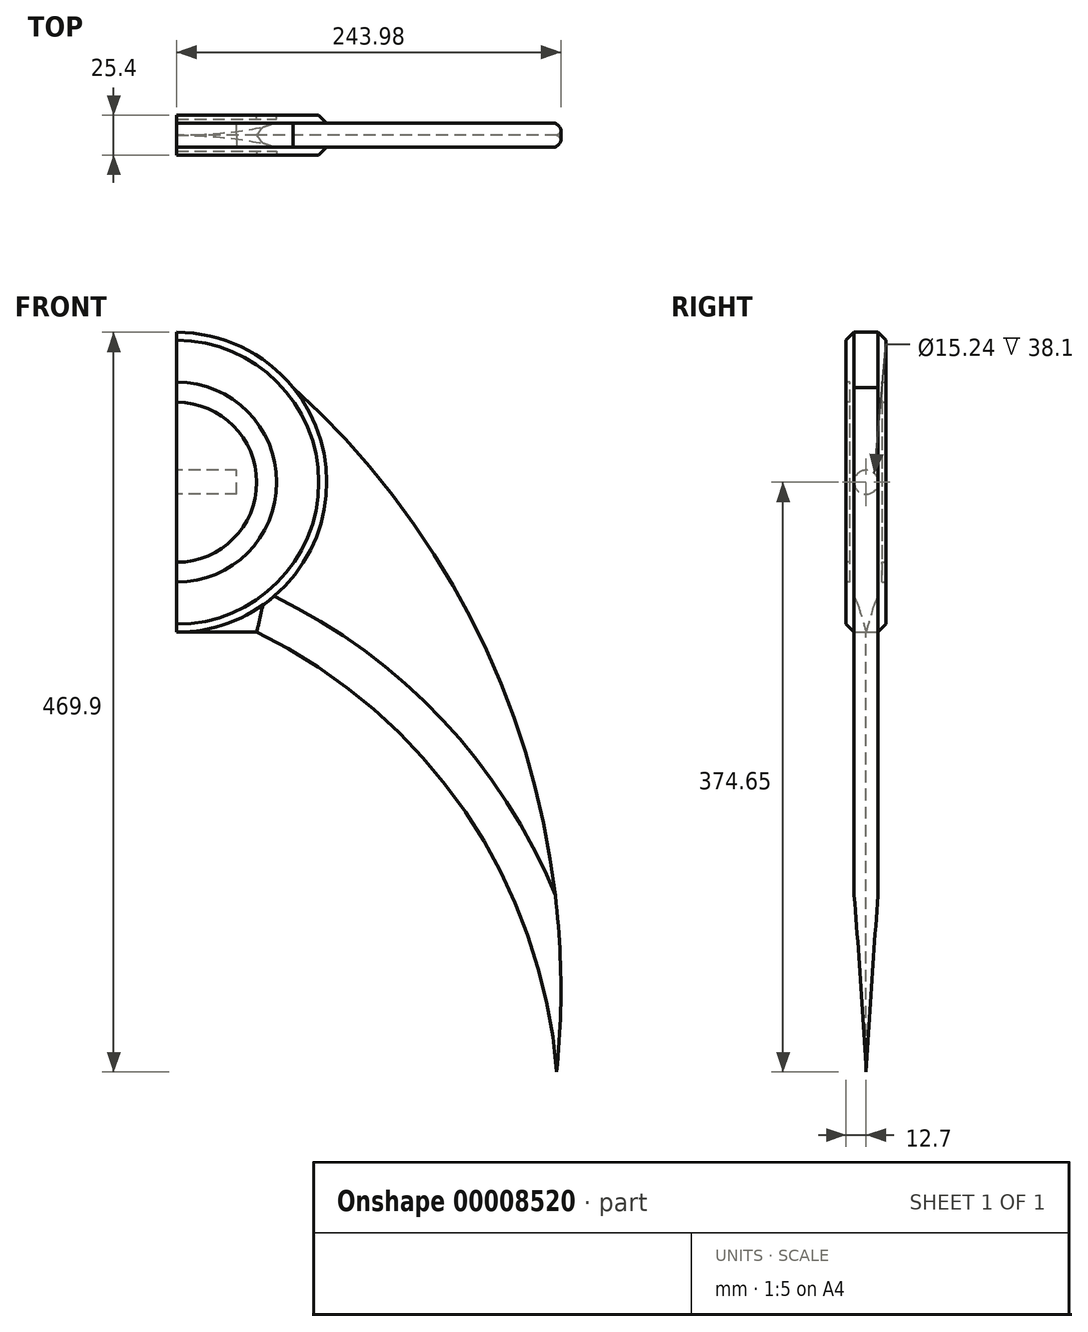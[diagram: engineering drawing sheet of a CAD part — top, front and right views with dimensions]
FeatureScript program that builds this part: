
annotation { "Feature Type Name" : "Feature", "Feature Type Description" : "" }
export const myFeature = defineFeature(function(context is Context, id is Id, definition is map)
    precondition{}
    {
        {
            var Q0;
            Q0=qCreatedBy(makeId("Right.planeOp"),FACE);
            var sketch = newSketch(context, id + "F0", { "sketchPlane" : qUnion([Q0])});
            skCircle(sketch, "E0", {"center": v(0, 0) * mm, "radius": 7.62 * mm});
            skSolve(sketch);
        }
        {
            var Q0;
            Q0=makeQuery(id+"F0.imprint","IMPRINT",FACE,{"disambiguationData":[TD([[makeQuery(id+"F0.imprint","IMPRINT",EDGE,{"derivedFrom":sQuery(id+"F0.wireOp",EDGE,"E0")}),1.0]])]});
            extrude(context, id + "F1", {"entities" : qUnion([Q0]), "depth" : 38.1 * mm});
        }
        {
            var Q0;
            Q0=qCreatedBy(makeId("Front.planeOp"),FACE);
            var sketch = newSketch(context, id + "F2", { "sketchPlane" : qUnion([Q0])});
            skLineSegment(sketch, "E1.0", {"start": v(38.1, 7.62) * mm, "end": v(38.1, -7.62) * mm});
            skArc(sketch, "E2", {"start": v(111.98, 60.11) * mm, "mid": v(79, 86.02) * mm, "end": v(38.1, 95.25) * mm});
            skLineSegment(sketch, "E3", {"start": v(38.1, 0) * mm, "end": v(38.1, 95.25) * mm});
            skLineSegment(sketch, "E4", {"start": v(38.1, 0) * mm, "end": v(38.1, -95.25) * mm});
            skLineSegment(sketch, "E5", {"start": v(38.1, -95.25) * mm, "end": v(88.9, -95.25) * mm});
            skArc(sketch, "E6", {"start": v(279.4, -374.65) * mm, "mid": v(221.44, -209.52) * mm, "end": v(88.9, -95.25) * mm});
            skArc(sketch, "E7", {"start": v(279.4, -374.65) * mm, "mid": v(247.68, -137.25) * mm, "end": v(111.98, 60.11) * mm});
            skSolve(sketch);
        }
        {
            var Q0;
            {var subQ3=sQuery(id+"F2.wireOp",EDGE,"E2");Q0=makeQuery(id+"F2.imprint","IMPRINT",FACE,{"disambiguationData":[TD([[makeQuery(id+"F2.imprint","IMPRINT",EDGE,{"derivedFrom":subQ3}),1.0]])]});}
            extrude(context, id + "F3", {"entities" : qUnion([Q0]), "operationType" : NewBodyOperationType.ADD, "depth" : 15.24 * mm, "symmetric" : true});
        }
        {
            var Q0;
            Q0=makeQuery(id+"F3.opExtrude","CAP_EDGE",EDGE,{"disambiguationData":[OSD([sQuery(id+"F2.wireOp",EDGE,"E6")])],"isStart":false});
            var Q1;
            Q1=makeQuery(id+"F3.opExtrude","CAP_EDGE",EDGE,{"disambiguationData":[OSD([sQuery(id+"F2.wireOp",EDGE,"E5")])],"isStart":false});
            chamfer(context, id + "F4", {"entities" : qUnion([Q0, Q1]), "chamferType" : ChamferType.TWO_OFFSETS, "width1" : 7.62 * mm, "oppositeDirection" : false, "width2" : 25.4 * mm, "tangentPropagation" : true});
        }
        {
            var Q0;
            Q0=makeQuery(id+"F3.opExtrude","CAP_EDGE",EDGE,{"disambiguationData":[OSD([sQuery(id+"F2.wireOp",EDGE,"E6")])],"isStart":true});
            var Q1;
            Q1=makeQuery(id+"F3.opExtrude","CAP_EDGE",EDGE,{"disambiguationData":[OSD([sQuery(id+"F2.wireOp",EDGE,"E5")])],"isStart":true});
            chamfer(context, id + "F5", {"entities" : qUnion([Q0, Q1]), "chamferType" : ChamferType.TWO_OFFSETS, "width1" : 25.4 * mm, "oppositeDirection" : false, "width2" : 7.62 * mm, "tangentPropagation" : true});
        }
        {
            var Q0;
            Q0=qCreatedBy(makeId("Front.planeOp"),FACE);
            var sketch = newSketch(context, id + "F6", { "sketchPlane" : qUnion([Q0])});
            skLineSegment(sketch, "E8.0", {"start": v(38.1, 0) * mm, "end": v(38.1, 95.25) * mm});
            skCircle(sketch, "E9", {"center": v(38.1, 0) * mm, "radius": 95.25 * mm});
            skLineSegment(sketch, "E10", {"start": v(38.1, 0) * mm, "end": v(38.1, -95.25) * mm});
            skSolve(sketch);
        }
        {
            var Q0;
            {var subQ2=sQuery(id+"F6.wireOp",EDGE,"E8.0");Q0=makeQuery(id+"F6.imprint","IMPRINT",FACE,{"disambiguationData":[TD([[makeQuery(id+"F6.imprint","IMPRINT",EDGE,{"derivedFrom":subQ2}),-1.0]])]});}
            extrude(context, id + "F7", {"entities" : qUnion([Q0]), "operationType" : NewBodyOperationType.ADD, "depth" : 25.4 * mm, "symmetric" : true});
        }
        {
            var Q0;
            Q0=makeQuery(id+"F7.opExtrude","CAP_EDGE",EDGE,{"disambiguationData":[OSD([sQuery(id+"F6.wireOp",EDGE,"E9")])],"isStart":false});
            var Q1;
            Q1=makeQuery(id+"F7.opExtrude","CAP_EDGE",EDGE,{"disambiguationData":[OSD([sQuery(id+"F6.wireOp",EDGE,"E9")])],"isStart":true});
            chamfer(context, id + "F8", {"entities" : qUnion([Q0, Q1]), "width" : 5.08 * mm, "tangentPropagation" : true});
        }
        {
            var Q0;
            Q0=makeQuery(id+"F7.opExtrude","CAP_FACE",FACE,{"disambiguationData":[OSD([sQuery(id+"F6.wireOp",EDGE,"E8.0"),sQuery(id+"F6.wireOp",EDGE,"E9"),sQuery(id+"F6.wireOp",EDGE,"E10")])],"isStart":false});
            var sketch = newSketch(context, id + "F9", { "sketchPlane" : qUnion([Q0])});
            skCircle(sketch, "E11", {"center": v(38.1, 0) * mm, "radius": 63.5 * mm});
            skCircle(sketch, "E12", {"center": v(38.1, 0) * mm, "radius": 50.8 * mm});
            skSolve(sketch);
        }
        {
            var Q0;
            {var subQ0=makeQuery(id+"F7.opExtrude","CAP_EDGE",EDGE,{"disambiguationData":[OSD([sQuery(id+"F6.wireOp",EDGE,"E8.0"),sQuery(id+"F6.wireOp",EDGE,"E10")])],"isStart":false});var subQ3=sQuery(id+"F9.wireOp",EDGE,"E11");var subQ6=makeQuery(id+"F9.imprint","INTERSECT",VERTEX,{"disambiguationData":[OD(0.0)],"derivedFrom":[subQ0,subQ3]});Q0=makeQuery(id+"F9.imprint","IMPRINT",FACE,{"disambiguationData":[TD([[makeQuery(id+"F9.imprint","IMPRINT",EDGE,{"disambiguationData":[TD([[subQ6,1.0]])],"derivedFrom":subQ3}),1.0]])]});}
            extrude(context, id + "F10", {"entities" : qUnion([Q0]), "operationType" : NewBodyOperationType.REMOVE, "oppositeDirection" : true, "depth" : 2.54 * mm});
        }
        {
            var Q0;
            Q0=makeQuery(id+"F7.opExtrude","CAP_FACE",FACE,{"disambiguationData":[OSD([sQuery(id+"F6.wireOp",EDGE,"E8.0"),sQuery(id+"F6.wireOp",EDGE,"E9"),sQuery(id+"F6.wireOp",EDGE,"E10")])],"isStart":true});
            var sketch = newSketch(context, id + "F11", { "sketchPlane" : qUnion([Q0])});
            skCircle(sketch, "E13", {"center": v(-38.1, 0) * mm, "radius": 63.5 * mm});
            skCircle(sketch, "E14", {"center": v(-38.1, 0) * mm, "radius": 50.8 * mm});
            skSolve(sketch);
        }
        {
            var Q0;
            {var subQ0=makeQuery(id+"F7.opExtrude","CAP_EDGE",EDGE,{"disambiguationData":[OSD([sQuery(id+"F6.wireOp",EDGE,"E8.0"),sQuery(id+"F6.wireOp",EDGE,"E10")])],"isStart":true});var subQ3=sQuery(id+"F11.wireOp",EDGE,"E13");var subQ6=makeQuery(id+"F11.imprint","INTERSECT",VERTEX,{"disambiguationData":[OD(0.0)],"derivedFrom":[subQ0,subQ3]});Q0=makeQuery(id+"F11.imprint","IMPRINT",FACE,{"disambiguationData":[TD([[makeQuery(id+"F11.imprint","IMPRINT",EDGE,{"disambiguationData":[TD([[subQ6,-1.0]])],"derivedFrom":subQ3}),1.0]])]});}
            extrude(context, id + "F12", {"entities" : qUnion([Q0]), "operationType" : NewBodyOperationType.REMOVE, "oppositeDirection" : true, "depth" : 2.54 * mm});
        }
        {
            var Q0;
            Q0=makeQuery(id+"F1.opExtrude","CAP_FACE",FACE,{"disambiguationData":[OSD([sQuery(id+"F0.wireOp",EDGE,"E0")])],"isStart":true});
            var sketch = newSketch(context, id + "F13", { "sketchPlane" : qUnion([Q0])});
            skSolve(sketch);
        }
        {
            var Q0;
            Q0 = qSketchRegion(id + "F13", true);
            var Q1;
            Q1=makeQuery(id+"F13.imprint","IMPRINT",FACE,{"disambiguationData":[TD([[makeQuery(id+"F13.imprint","IMPRINT",EDGE,{"derivedFrom":makeQuery(id+"F1.opExtrude","CAP_EDGE",EDGE,{"disambiguationData":[OSD([sQuery(id+"F0.wireOp",EDGE,"E0")])],"isStart":true})}),-1.0]])]});
            extrude(context, id + "F14", {"entities" : qUnion([Q0, Q1]), "operationType" : NewBodyOperationType.REMOVE, "oppositeDirection" : true, "depth" : 76.2 * mm});
        }
    });
